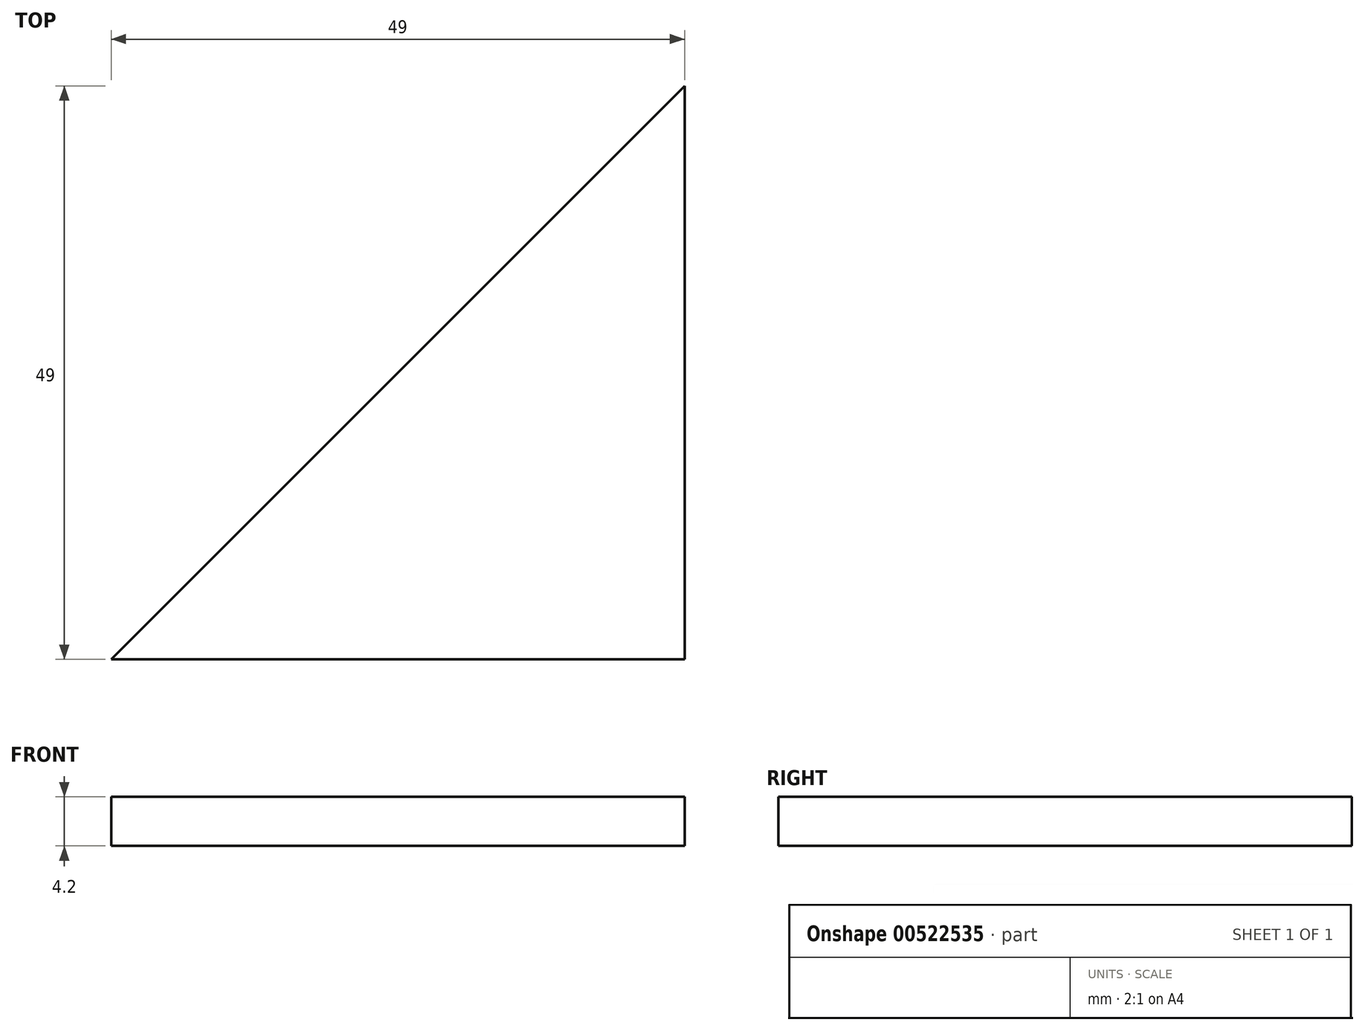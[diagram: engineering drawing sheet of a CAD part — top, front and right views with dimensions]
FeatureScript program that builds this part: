
annotation { "Feature Type Name" : "Feature", "Feature Type Description" : "" }
export const myFeature = defineFeature(function(context is Context, id is Id, definition is map)
    precondition{}
    {
        {
            var Q0;
            Q0=qCreatedBy(makeId("Top.planeOp"),FACE);
            var sketch = newSketch(context, id + "F0", { "sketchPlane" : qUnion([Q0])});
            skLineSegment(sketch, "E0", {"start": v(0, 0) * mm, "end": v(0, 49) * mm});
            skLineSegment(sketch, "E1", {"start": v(0, 49) * mm, "end": v(-49, 0) * mm});
            skLineSegment(sketch, "E2", {"start": v(-49, 0) * mm, "end": v(0, 0) * mm});
            skSolve(sketch);
        }
        {
            var Q0;
            Q0=makeQuery(id+"F0.imprint","IMPRINT",FACE,{"disambiguationData":[TD([[makeQuery(id+"F0.imprint","IMPRINT",EDGE,{"derivedFrom":sQuery(id+"F0.wireOp",EDGE,"E0")}),1.0]])]});
            extrude(context, id + "F1", {"entities" : qUnion([Q0]), "depth" : 4.2 * mm, "offsetDistance" : 25 * mm});
        }
    });
